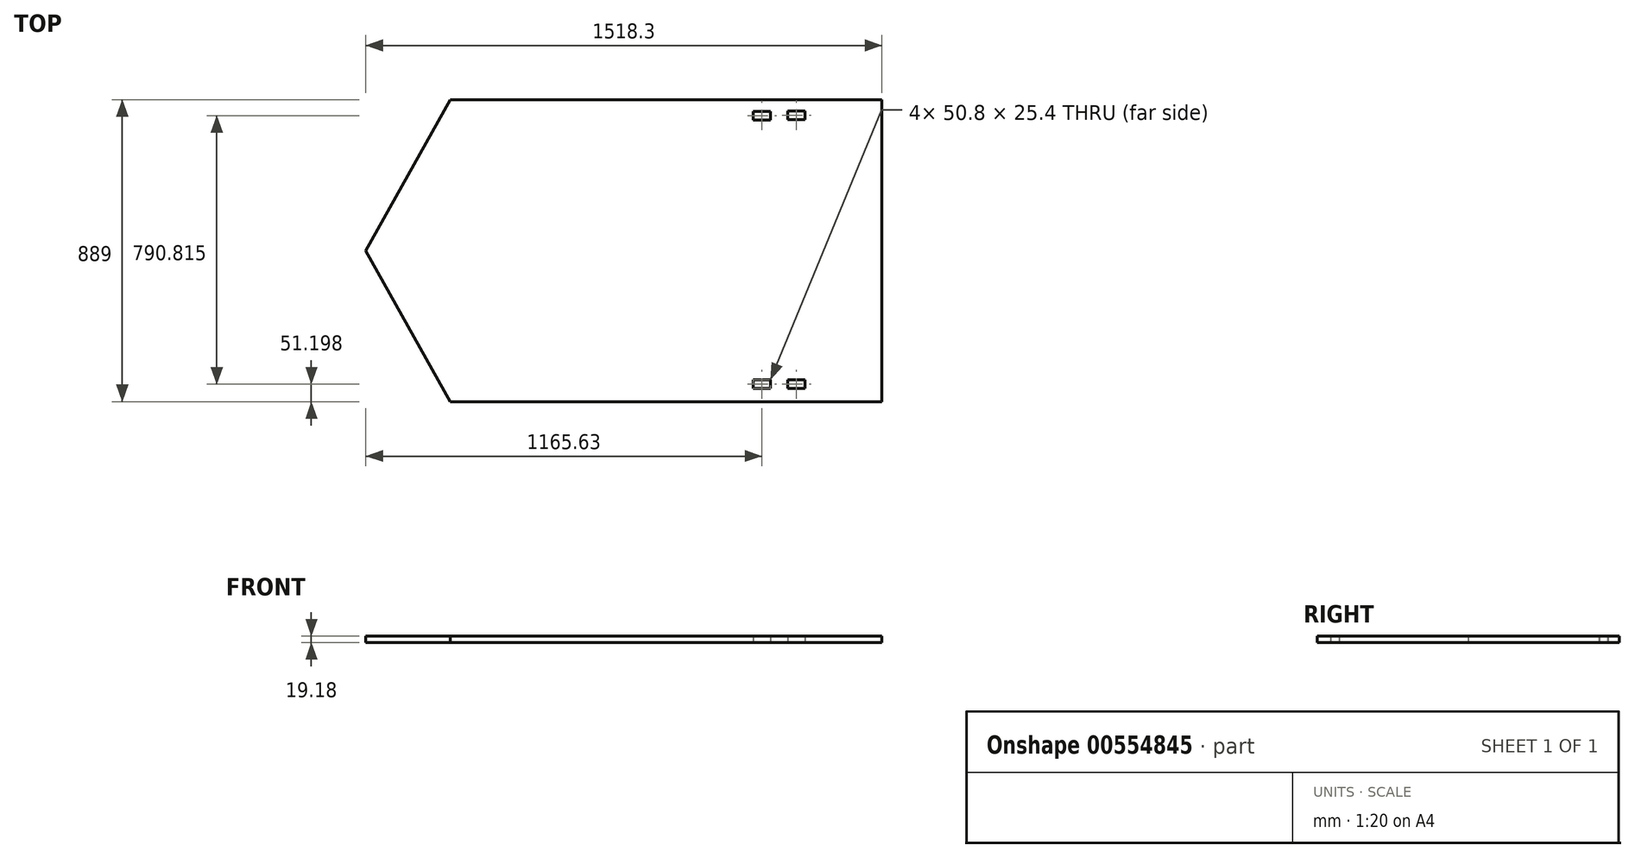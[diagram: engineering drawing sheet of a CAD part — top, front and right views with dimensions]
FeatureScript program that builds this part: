
annotation { "Feature Type Name" : "Feature", "Feature Type Description" : "" }
export const myFeature = defineFeature(function(context is Context, id is Id, definition is map)
    precondition{}
    {
        {
            var Q0;
            Q0=qCreatedBy(makeId("Top.planeOp"),FACE);
            var sketch = newSketch(context, id + "F0", { "sketchPlane" : qUnion([Q0])});
            skLineSegment(sketch, "E0.bottom", {"start": v(-327.73, 485.91) * mm, "end": v(942.27, 485.91) * mm});
            skLineSegment(sketch, "E0.top", {"start": v(-327.73, -403.09) * mm, "end": v(942.27, -403.09) * mm});
            skLineSegment(sketch, "E0.right", {"start": v(942.27, 485.91) * mm, "end": v(942.27, -403.09) * mm});
            skLineSegment(sketch, "E1", {"start": v(564.2, 426.22) * mm, "end": v(564.2, 451.62) * mm});
            skLineSegment(sketch, "E2", {"start": v(716.6, 452.46) * mm, "end": v(716.6, 427.06) * mm});
            skLineSegment(sketch, "E3", {"start": v(564.2, 426.22) * mm, "end": v(615, 426.22) * mm});
            skLineSegment(sketch, "E4", {"start": v(716.6, 427.06) * mm, "end": v(665.8, 427.06) * mm});
            skLineSegment(sketch, "E5", {"start": v(615, 426.22) * mm, "end": v(615, 451.62) * mm});
            skLineSegment(sketch, "E6", {"start": v(665.8, 427.06) * mm, "end": v(665.8, 452.46) * mm});
            skLineSegment(sketch, "E7", {"start": v(564.2, 451.62) * mm, "end": v(615, 451.62) * mm});
            skLineSegment(sketch, "E8", {"start": v(665.8, 452.46) * mm, "end": v(716.6, 452.46) * mm});
            skLineSegment(sketch, "E9", {"start": v(615, -364.6) * mm, "end": v(615, -339.2) * mm});
            skLineSegment(sketch, "E10", {"start": v(564.2, -364.6) * mm, "end": v(564.2, -339.2) * mm});
            skLineSegment(sketch, "E11", {"start": v(564.2, -364.6) * mm, "end": v(615, -364.6) * mm});
            skLineSegment(sketch, "E12", {"start": v(564.2, -339.2) * mm, "end": v(615, -339.2) * mm});
            skLineSegment(sketch, "E13", {"start": v(665.8, -364.6) * mm, "end": v(665.8, -339.2) * mm});
            skLineSegment(sketch, "E14", {"start": v(665.8, -339.2) * mm, "end": v(716.6, -339.2) * mm});
            skLineSegment(sketch, "E15", {"start": v(716.6, -339.2) * mm, "end": v(716.6, -364.6) * mm});
            skLineSegment(sketch, "E16", {"start": v(716.6, -364.6) * mm, "end": v(665.8, -364.6) * mm});
            skLineSegment(sketch, "E17", {"start": v(-327.73, 485.91) * mm, "end": v(-576.03, 41.41) * mm});
            skLineSegment(sketch, "E18", {"start": v(-327.73, -403.09) * mm, "end": v(-576.03, 41.41) * mm});
            skPoint(sketch, "E19.end.orphan", {"position": v(818.2, 427.06) * mm});
            skPoint(sketch, "E19.start.orphan", {"position": v(818.2, 452.46) * mm});
            skPoint(sketch, "E20.end.orphan", {"position": v(767.4, 452.46) * mm});
            skPoint(sketch, "E20.start.orphan", {"position": v(767.4, 427.06) * mm});
            skPoint(sketch, "E21.end.orphan", {"position": v(767.4, -364.6) * mm});
            skPoint(sketch, "E21.start.orphan", {"position": v(767.4, -339.2) * mm});
            skPoint(sketch, "E22.end.orphan", {"position": v(818.2, -339.2) * mm});
            skPoint(sketch, "E22.start.orphan", {"position": v(818.2, -364.6) * mm});
            skSolve(sketch);
        }
        {
            var Q0;
            Q0=qSketchRegion(id+"F0",true);
            extrude(context, id + "F1", {"entities" : qUnion([Q0]), "depth" : 19.18 * mm, "offsetDistance" : 25.4 * mm});
        }
    });
